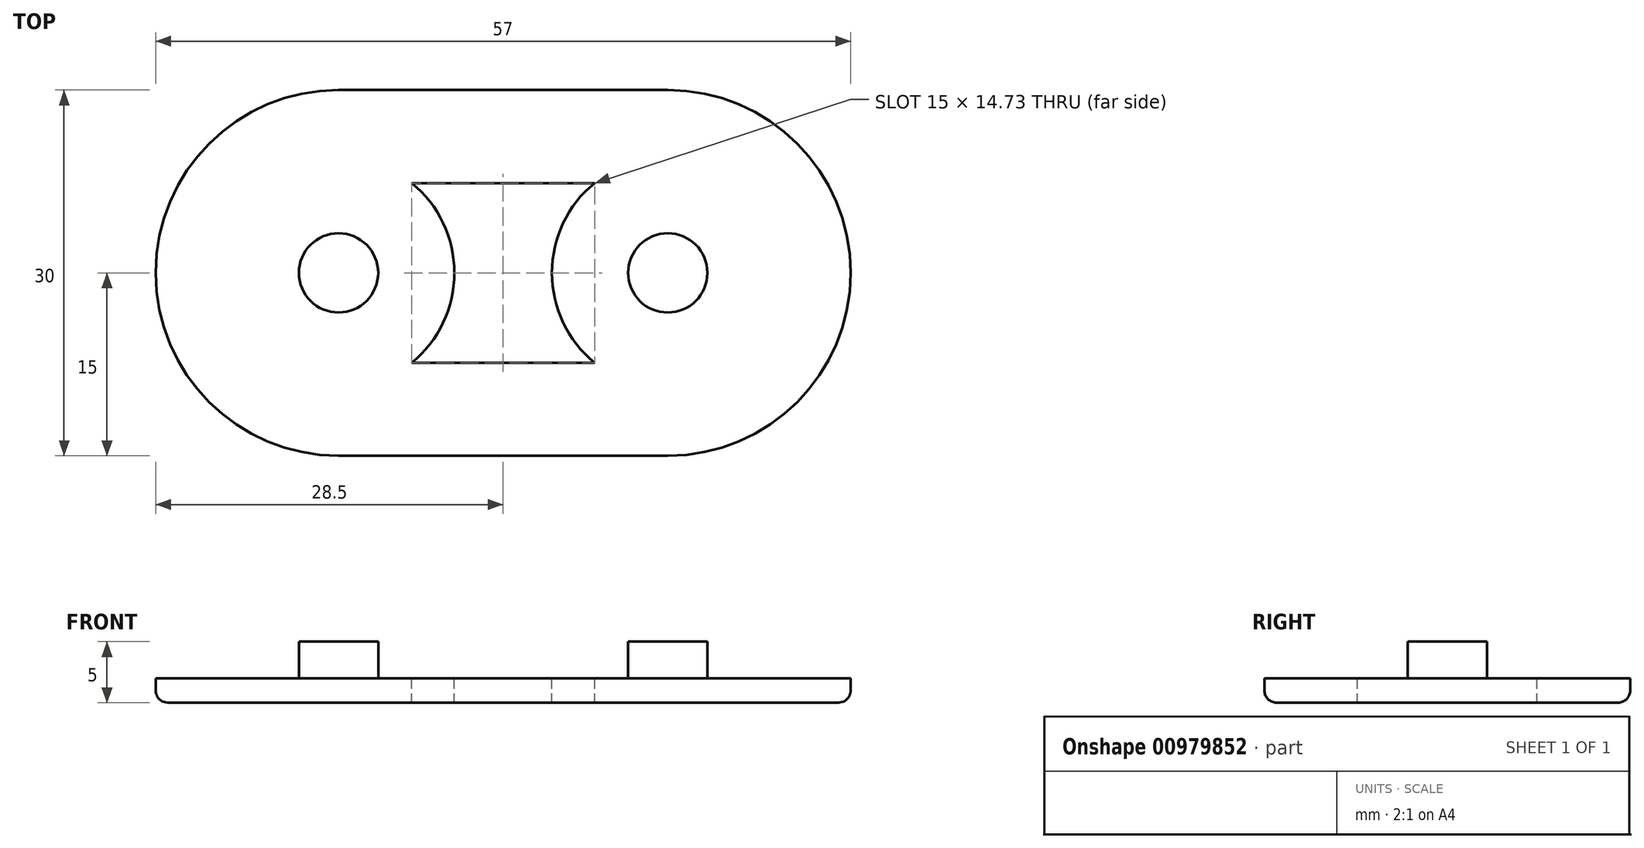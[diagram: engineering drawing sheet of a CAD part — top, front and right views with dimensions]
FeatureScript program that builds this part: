
annotation { "Feature Type Name" : "Feature", "Feature Type Description" : "" }
export const myFeature = defineFeature(function(context is Context, id is Id, definition is map)
    precondition{}
    {
        {
            var Q0;
            Q0=qCreatedBy(makeId("Top.planeOp"),FACE);
            var sketch = newSketch(context, id + "F0", { "sketchPlane" : qUnion([Q0])});
            skCircle(sketch, "E0", {"center": v(-15, 0) * mm, "radius": 15 * mm});
            skCircle(sketch, "E1", {"center": v(12, 0) * mm, "radius": 15 * mm});
            skLineSegment(sketch, "E2", {"start": v(-15, 0) * mm, "end": v(12, 0) * mm, "construction": true});
            skLineSegment(sketch, "E3", {"start": v(-15, -15) * mm, "end": v(12, -15) * mm});
            skLineSegment(sketch, "E4", {"start": v(-15, 15) * mm, "end": v(12, 15) * mm});
            skSolve(sketch);
        }
        {
            var Q0;
            {var subQ0=sQuery(id+"F0.wireOp",EDGE,"E0");var subQ1=makeQuery(id+"F0.imprint","INTERSECT",VERTEX,{"derivedFrom":[subQ0,sQuery(id+"F0.wireOp",EDGE,"E4")]});Q0=makeQuery(id+"F0.imprint","IMPRINT",FACE,{"disambiguationData":[TD([[makeQuery(id+"F0.imprint","IMPRINT",EDGE,{"disambiguationData":[TD([[subQ1,1.0]])],"derivedFrom":subQ0}),1.0]])]});}
            var Q1;
            {var subQ0=sQuery(id+"F0.wireOp",EDGE,"E4");Q1=makeQuery(id+"F0.imprint","IMPRINT",FACE,{"disambiguationData":[TD([[makeQuery(id+"F0.imprint","IMPRINT",EDGE,{"derivedFrom":subQ0}),-1.0]])]});}
            var Q2;
            {var subQ0=sQuery(id+"F0.wireOp",EDGE,"E1");var subQ1=sQuery(id+"F0.wireOp",EDGE,"E0");var subQ2=makeQuery(id+"F0.imprint","INTERSECT",VERTEX,{"disambiguationData":[OD(0.0)],"derivedFrom":[subQ1,subQ0]});Q2=makeQuery(id+"F0.imprint","IMPRINT",FACE,{"disambiguationData":[TD([[makeQuery(id+"F0.imprint","IMPRINT",EDGE,{"disambiguationData":[TD([[subQ2,1.0]])],"derivedFrom":subQ1}),-1.0]])]});}
            var Q3;
            {var subQ0=sQuery(id+"F0.wireOp",EDGE,"E1");var subQ1=sQuery(id+"F0.wireOp",EDGE,"E0");var subQ2=makeQuery(id+"F0.imprint","INTERSECT",VERTEX,{"disambiguationData":[OD(0.0)],"derivedFrom":[subQ1,subQ0]});Q3=makeQuery(id+"F0.imprint","IMPRINT",FACE,{"disambiguationData":[TD([[makeQuery(id+"F0.imprint","IMPRINT",EDGE,{"disambiguationData":[TD([[subQ2,1.0]])],"derivedFrom":subQ1}),1.0]])]});}
            var Q4;
            {var subQ0=sQuery(id+"F0.wireOp",EDGE,"E3");Q4=makeQuery(id+"F0.imprint","IMPRINT",FACE,{"disambiguationData":[TD([[makeQuery(id+"F0.imprint","IMPRINT",EDGE,{"derivedFrom":subQ0}),1.0]])]});}
            var Q5;
            {var subQ0=sQuery(id+"F0.wireOp",EDGE,"E1");var subQ1=makeQuery(id+"F0.imprint","INTERSECT",VERTEX,{"derivedFrom":[subQ0,sQuery(id+"F0.wireOp",EDGE,"E4")]});Q5=makeQuery(id+"F0.imprint","IMPRINT",FACE,{"disambiguationData":[TD([[makeQuery(id+"F0.imprint","IMPRINT",EDGE,{"disambiguationData":[TD([[subQ1,-1.0]])],"derivedFrom":subQ0}),1.0]])]});}
            extrude(context, id + "F1", {"entities" : qUnion([Q0, Q1, Q2, Q3, Q4, Q5]), "depth" : 2 * mm, "offsetDistance" : 25 * mm});
        }
        {
            var Q0;
            Q0=makeQuery(id+"F1.opExtrude","CAP_FACE",FACE,{"disambiguationData":[OSD([sQuery(id+"F0.wireOp",EDGE,"E0"),sQuery(id+"F0.wireOp",EDGE,"E1"),sQuery(id+"F0.wireOp",EDGE,"E3"),sQuery(id+"F0.wireOp",EDGE,"E4")])],"isStart":false});
            var sketch = newSketch(context, id + "F2", { "sketchPlane" : qUnion([Q0])});
            skArc(sketch, "E5.0", {"start": v(12, -15) * mm, "mid": v(27, 0) * mm, "end": v(12, 15) * mm, "construction": true});
            skArc(sketch, "E6.0", {"start": v(-15, 15) * mm, "mid": v(-30, 0) * mm, "end": v(-15, -15) * mm, "construction": true});
            skCircle(sketch, "E7", {"center": v(-15, 0) * mm, "radius": 5.5 * mm});
            skCircle(sketch, "E8", {"center": v(12, 0) * mm, "radius": 5.5 * mm});
            skCircle(sketch, "E9.0", {"center": v(-15, 0) * mm, "radius": 3.5 * mm});
            skCircle(sketch, "E10.0", {"center": v(12, 0) * mm, "radius": 3.5 * mm});
            skCircle(sketch, "E11", {"center": v(-15, 0) * mm, "radius": 3.25 * mm});
            skCircle(sketch, "E12", {"center": v(12, 0) * mm, "radius": 3.25 * mm});
            skSolve(sketch);
        }
        {
            var Q0;
            Q0=makeQuery(id+"F2.imprint","IMPRINT",FACE,{"disambiguationData":[TD([[makeQuery(id+"F2.imprint","IMPRINT",EDGE,{"derivedFrom":sQuery(id+"F2.wireOp",EDGE,"E11")}),1.0]])]});
            var Q1;
            Q1=makeQuery(id+"F2.imprint","IMPRINT",FACE,{"disambiguationData":[TD([[makeQuery(id+"F2.imprint","IMPRINT",EDGE,{"derivedFrom":sQuery(id+"F2.wireOp",EDGE,"E12")}),1.0]])]});
            extrude(context, id + "F3", {"entities" : qUnion([Q0, Q1]), "operationType" : NewBodyOperationType.ADD, "depth" : 3 * mm, "offsetDistance" : 25 * mm});
        }
        {
            var Q0;
            {var subQ0=sQuery(id+"F0.wireOp",EDGE,"E3");var subQ1=sQuery(id+"F0.wireOp",EDGE,"E1");var subQ2=sQuery(id+"F0.wireOp",EDGE,"E4");var subQ3=sQuery(id+"F0.wireOp",EDGE,"E0");Q0=makeQuery(id+"F3.boolean.opBoolean","SPLIT",FACE,{"disambiguationData":[TD([makeQuery(id+"F1.opExtrude","SWEPT_FACE",FACE,{"disambiguationData":[OSD([subQ3])]})])],"derivedFrom":makeQuery(id+"F1.opExtrude","CAP_FACE",FACE,{"disambiguationData":[OSD([subQ3,subQ1,subQ0,subQ2])],"isStart":false})});}
            var sketch = newSketch(context, id + "F4", { "sketchPlane" : qUnion([Q0])});
            skCircle(sketch, "E13.0", {"center": v(-15, 0) * mm, "radius": 9.5 * mm});
            skCircle(sketch, "E14.0", {"center": v(12, 0) * mm, "radius": 9.5 * mm});
            skLineSegment(sketch, "E15", {"start": v(-9, -7.37) * mm, "end": v(6, -7.37) * mm});
            skLineSegment(sketch, "E16", {"start": v(6, -7.37) * mm, "end": v(6, 7.37) * mm});
            skLineSegment(sketch, "E17", {"start": v(6, 7.37) * mm, "end": v(-9, 7.37) * mm});
            skSolve(sketch);
        }
        {
            var Q0;
            {var subQ0=sQuery(id+"F4.wireOp",EDGE,"E15");Q0=makeQuery(id+"F4.imprint","IMPRINT",FACE,{"disambiguationData":[TD([[makeQuery(id+"F4.imprint","IMPRINT",EDGE,{"derivedFrom":subQ0}),1.0]])]});}
            extrude(context, id + "F5", {"entities" : qUnion([Q0]), "operationType" : NewBodyOperationType.REMOVE, "endBound" : BoundingType.UP_TO_NEXT, "oppositeDirection" : true, "depth" : 25 * mm, "offsetDistance" : 25 * mm});
        }
        {
            var Q0;
            Q0=makeQuery(id+"F5.boolean.opBoolean","COPY",EDGE,{"derivedFrom":makeQuery(id+"F5.opExtrude","CAP_EDGE",EDGE,{"disambiguationData":[OSD([sQuery(id+"F4.wireOp",EDGE,"E14.0")])],"isStart":false})});
            var Q1;
            Q1=makeQuery(id+"F5.boolean.opBoolean","COPY",EDGE,{"derivedFrom":makeQuery(id+"F5.opExtrude","CAP_EDGE",EDGE,{"disambiguationData":[OSD([sQuery(id+"F4.wireOp",EDGE,"E13.0")])],"isStart":false})});
            var Q2;
            Q2=makeQuery(id+"F1.opExtrude","CAP_EDGE",EDGE,{"disambiguationData":[OSD([sQuery(id+"F0.wireOp",EDGE,"E3")])],"isStart":true});
            var Q3;
            Q3=makeQuery(id+"F1.opExtrude","CAP_EDGE",EDGE,{"disambiguationData":[OSD([sQuery(id+"F0.wireOp",EDGE,"E1")])],"isStart":true});
            var Q4;
            Q4=makeQuery(id+"F1.opExtrude","CAP_EDGE",EDGE,{"disambiguationData":[OSD([sQuery(id+"F0.wireOp",EDGE,"E0")])],"isStart":true});
            var Q5;
            Q5=makeQuery(id+"F1.opExtrude","CAP_EDGE",EDGE,{"disambiguationData":[OSD([sQuery(id+"F0.wireOp",EDGE,"E4")])],"isStart":true});
            fillet(context, id + "F6", {"entities" : qUnion([Q0, Q1, Q2, Q3, Q4, Q5]), "radius" : 1 * mm, "tangentPropagation" : true, "allowEdgeOverflow" : false});
        }
    });
